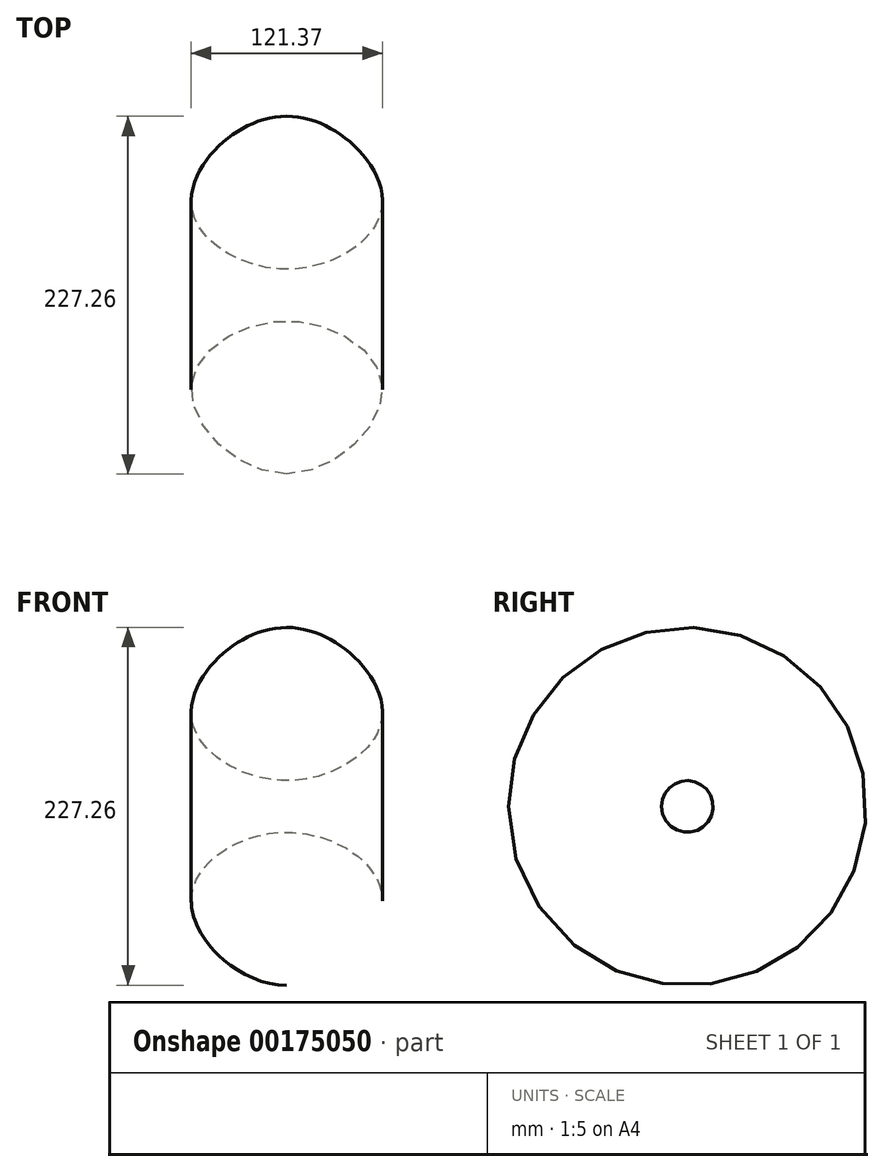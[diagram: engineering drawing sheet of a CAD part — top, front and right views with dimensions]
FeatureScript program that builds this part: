
annotation { "Feature Type Name" : "Feature", "Feature Type Description" : "" }
export const myFeature = defineFeature(function(context is Context, id is Id, definition is map)
    precondition{}
    {
        {
            var Q0;
            Q0=qCreatedBy(makeId("Top.planeOp"),FACE);
            var sketch = newSketch(context, id + "F0", { "sketchPlane" : qUnion([Q0])});
            skFitSpline(sketch, "E0", {"points": [v(0, -54.81) * mm, v(-60.5, 0) * mm, v(0, 42.44) * mm, v(60.83, 0) * mm, v(0, -54.81) * mm]});
            skLineSegment(sketch, "E1", {"start": v(-19.05, 58.82) * mm, "end": v(19.05, 58.82) * mm});
            skSolve(sketch);
        }
        {
            var Q0;
            Q0=makeQuery(id+"F0.imprint","IMPRINT",FACE,{"disambiguationData":[TD([[makeQuery(id+"F0.imprint","IMPRINT",EDGE,{"derivedFrom":sQuery(id+"F0.wireOp",EDGE,"E0")}),-1.0]])]});
            var Q1;
            Q1=sQuery(id+"F0.wireOp",EDGE,"E1");
            revolve(context, id + "F1", {"entities" : qUnion([Q0]), "axis" : qUnion([Q1]), "revolveType" : RevolveType.FULL});
        }
    });
